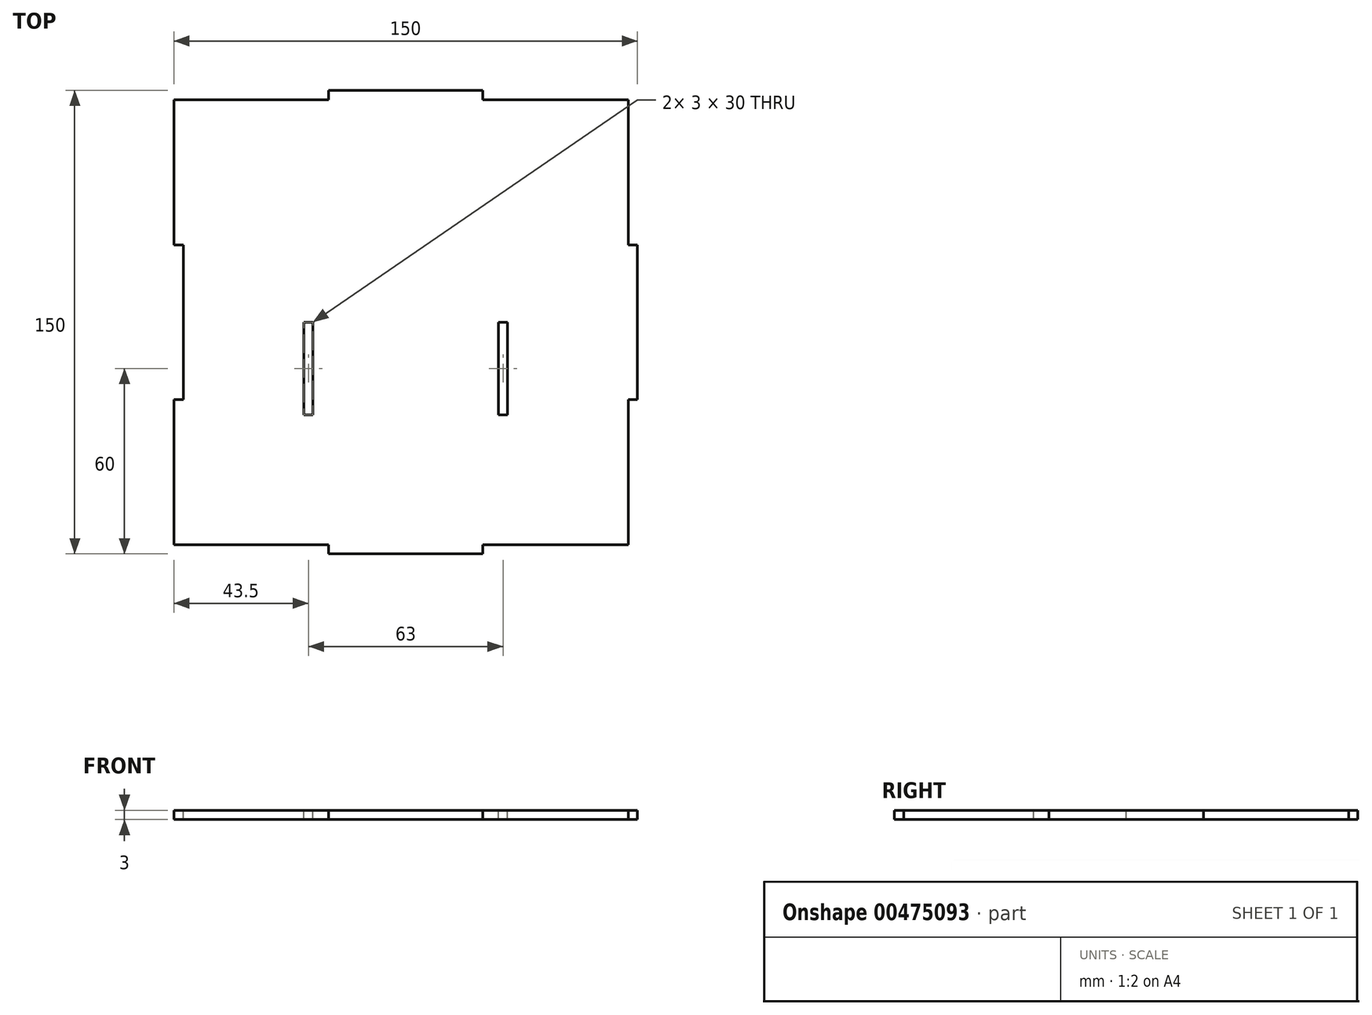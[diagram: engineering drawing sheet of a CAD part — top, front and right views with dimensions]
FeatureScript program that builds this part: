
annotation { "Feature Type Name" : "Feature", "Feature Type Description" : "" }
export const myFeature = defineFeature(function(context is Context, id is Id, definition is map)
    precondition{}
    {
        {
            var Q0;
            Q0=qCreatedBy(makeId("Top.planeOp"),FACE);
            var sketch = newSketch(context, id + "F0", { "sketchPlane" : qUnion([Q0])});
            skLineSegment(sketch, "E0.bottom", {"start": v(25, 75) * mm, "end": v(-25, 75) * mm});
            skLineSegment(sketch, "E0.top", {"start": v(25, -75) * mm, "end": v(-25, -75) * mm});
            skLineSegment(sketch, "E0.left", {"start": v(75, 25) * mm, "end": v(75, -25) * mm});
            skLineSegment(sketch, "E0.right", {"start": v(-75, 72) * mm, "end": v(-75, 25) * mm});
            skPoint(sketch, "E0.middle", {"position": v(0, 0) * mm});
            skLineSegment(sketch, "E1", {"start": v(-75, 72) * mm, "end": v(-25, 72) * mm});
            skLineSegment(sketch, "E2", {"start": v(-25, 72) * mm, "end": v(-25, 75) * mm});
            skLineSegment(sketch, "E3", {"start": v(72, 72) * mm, "end": v(25, 72) * mm});
            skLineSegment(sketch, "E4", {"start": v(25, 72) * mm, "end": v(25, 75) * mm});
            skPoint(sketch, "E5.orphan", {"position": v(-75, 75) * mm});
            skPoint(sketch, "E6.orphan", {"position": v(75, 75) * mm});
            skLineSegment(sketch, "E7", {"start": v(-75, -72) * mm, "end": v(-25, -72) * mm});
            skLineSegment(sketch, "E8", {"start": v(-25, -72) * mm, "end": v(-25, -75) * mm});
            skLineSegment(sketch, "E9", {"start": v(72, -72) * mm, "end": v(25, -72) * mm});
            skLineSegment(sketch, "E10", {"start": v(25, -72) * mm, "end": v(25, -75) * mm});
            skPoint(sketch, "E11.orphan", {"position": v(-75, -75) * mm});
            skPoint(sketch, "E12.orphan", {"position": v(75, -75) * mm});
            skLineSegment(sketch, "E13", {"start": v(-75, 25) * mm, "end": v(-72, 25) * mm});
            skLineSegment(sketch, "E14", {"start": v(-72, 25) * mm, "end": v(-72, -25) * mm});
            skLineSegment(sketch, "E15", {"start": v(-72, -25) * mm, "end": v(-75, -25) * mm});
            skLineSegment(sketch, "E16.trimOffspring", {"start": v(-75, -25) * mm, "end": v(-75, -72) * mm});
            skLineSegment(sketch, "E17", {"start": v(72, 72) * mm, "end": v(72, 25) * mm});
            skLineSegment(sketch, "E18", {"start": v(72, 25) * mm, "end": v(75, 25) * mm});
            skLineSegment(sketch, "E19", {"start": v(72, -72) * mm, "end": v(72, -25) * mm});
            skLineSegment(sketch, "E20", {"start": v(72, -25) * mm, "end": v(75, -25) * mm});
            skPoint(sketch, "E21.start.orphan", {"position": v(75, 72) * mm});
            skLineSegment(sketch, "E22", {"start": v(0, 0) * mm, "end": v(0, 40) * mm});
            skLineSegment(sketch, "E23", {"start": v(0, 40) * mm, "end": v(-35, 40) * mm});
            skLineSegment(sketch, "E24", {"start": v(0, 40) * mm, "end": v(35, 40) * mm});
            skLineSegment(sketch, "E25.bottom", {"start": v(-25, 52.5) * mm, "end": v(-45, 52.5) * mm});
            skLineSegment(sketch, "E25.top", {"start": v(-25, 27.5) * mm, "end": v(-45, 27.5) * mm});
            skLineSegment(sketch, "E25.left", {"start": v(-25, 52.5) * mm, "end": v(-25, 27.5) * mm});
            skLineSegment(sketch, "E25.right", {"start": v(-45, 52.5) * mm, "end": v(-45, 27.5) * mm});
            skPoint(sketch, "E25.middle", {"position": v(-35, 40) * mm});
            skLineSegment(sketch, "E26.bottom", {"start": v(45, 52.5) * mm, "end": v(25, 52.5) * mm});
            skLineSegment(sketch, "E26.top", {"start": v(45, 27.5) * mm, "end": v(25, 27.5) * mm});
            skLineSegment(sketch, "E26.left", {"start": v(45, 52.5) * mm, "end": v(45, 27.5) * mm});
            skLineSegment(sketch, "E26.right", {"start": v(25, 52.5) * mm, "end": v(25, 27.5) * mm});
            skPoint(sketch, "E26.middle", {"position": v(35, 40) * mm});
            skLineSegment(sketch, "E27", {"start": v(0, 0) * mm, "end": v(-30, 0) * mm});
            skLineSegment(sketch, "E28", {"start": v(0, 0) * mm, "end": v(30, 0) * mm});
            skLineSegment(sketch, "E29.bottom", {"start": v(-30, 0) * mm, "end": v(-33, 0) * mm});
            skLineSegment(sketch, "E29.top", {"start": v(-30, -30) * mm, "end": v(-33, -30) * mm});
            skLineSegment(sketch, "E29.left", {"start": v(-30, 0) * mm, "end": v(-30, -30) * mm});
            skLineSegment(sketch, "E29.right", {"start": v(-33, 0) * mm, "end": v(-33, -30) * mm});
            skLineSegment(sketch, "E30.bottom", {"start": v(30, 0) * mm, "end": v(33, 0) * mm});
            skLineSegment(sketch, "E30.top", {"start": v(30, -30) * mm, "end": v(33, -30) * mm});
            skLineSegment(sketch, "E30.left", {"start": v(30, 0) * mm, "end": v(30, -30) * mm});
            skLineSegment(sketch, "E30.right", {"start": v(33, 0) * mm, "end": v(33, -30) * mm});
            skSolve(sketch);
        }
        {
            var Q0;
            Q0=makeQuery(id+"F0.imprint","IMPRINT",FACE,{"disambiguationData":[TD([[makeQuery(id+"F0.imprint","IMPRINT",EDGE,{"derivedFrom":sQuery(id+"F0.wireOp",EDGE,"E0.bottom")}),1.0]])]});
            var Q1;
            {var subQ3=sQuery(id+"F0.wireOp",EDGE,"E25.bottom");Q1=makeQuery(id+"F0.imprint","IMPRINT",FACE,{"disambiguationData":[TD([[makeQuery(id+"F0.imprint","IMPRINT",EDGE,{"derivedFrom":subQ3}),1.0]])]});}
            var Q2;
            {var subQ1=sQuery(id+"F0.wireOp",EDGE,"E26.bottom");Q2=makeQuery(id+"F0.imprint","IMPRINT",FACE,{"disambiguationData":[TD([[makeQuery(id+"F0.imprint","IMPRINT",EDGE,{"derivedFrom":subQ1}),1.0]])]});}
            extrude(context, id + "F1", {"entities" : qUnion([Q0, Q1, Q2]), "oppositeDirection" : true, "depth" : 3 * mm});
        }
    });
